SOLIDWORKS PART (.sldprt)
format: sldprt  version: not decoded by parser v0  size: 266,240 bytes
history: native  units: mm
features: sketch x13, extrude x7, cut_extrude x6, fillet x1 + 8 further entries (+9 scaffold rows collapsed; 10 parser-record rows omitted)
feature tree (54):
  scaffold x9  (default folders/planes/origin — collapsed)
  parser-record x10  (decoder bookkeeping rows leaked as tree rows — omitted from the tree; the rows remain in map.json)
  "ID2"
  "ID3"
  sketch  "Sketch1"  dims[D1=38.1mm D2=38.1mm]
  extrude  "Base-Extrude"  Depth=38.1mm
  sketch  "Sketch3"  dims[D1=8.4328mm]
  cut_extrude  "Cut-Extrude1"  [1 undecoded]
  sketch  "Sketch4"  dims[D1=8.4328mm D2=~5.344011mm]
  cut_extrude  "Cut-Extrude2"  [1 undecoded]
  sketch  "Sketch5"  dims[D1=8.4328mm]
  cut_extrude  "Cut-Extrude3"  [1 undecoded]
  sketch  "Sketch8"  dims[D1=13.081mm]
  cut_extrude  "Cut-Extrude4"  Depth=31.75mm
  sketch  "Sketch11"  dims[D1=13.081mm]
  cut_extrude  "Cut-Extrude7"  Depth=31.75mm
  sketch  "Sketch12"  dims[D1=13.081mm]
  cut_extrude  "Cut-Extrude8"  Depth=31.75mm
  sketch  "Sketch13"  dims[D1=5.08mm D2=8.128mm D3=14.986mm]
  extrude  "Boss-Extrude1"  Depth=2.54mm
  sketch  "Sketch15"  dims[D1=5.08mm]
  extrude  "Boss-Extrude2"  Depth=2.54mm
  sketch  "Sketch16"  dims[D1=5.08mm D2=8.128mm D3=14.986mm]
  extrude  "Boss-Extrude3"  Depth=2.54mm
  sketch  "Sketch17"  dims[D1=5.08mm D2=5.08mm]
  extrude  "Boss-Extrude4"  Depth=2.54mm
  sketch  "Sketch18"  dims[D1=5.08mm D2=8.128mm D3=14.986mm]
  extrude  "Boss-Extrude5"  Depth=2.54mm
  sketch  "Sketch19"  dims[D1=5.08mm]
  extrude  "Boss-Extrude6"  Depth=2.54mm
  fillet  "Fillet1"  Radius=1.27mm
  "ID4"
  "ID5"
  "ID6"
  "ID7"
  "ID8"
  "ID9"
decode coverage: 24 of 27 modeling features carry decoded parameters; 8 rows unclassified (native names shown)
note: ~ marks probable driven/reference dimensions
note: 3 parameter values undecoded
summary: no parameter record found for 3 features
note: suppression state not decoded; provenance and decode notes live in map.json
